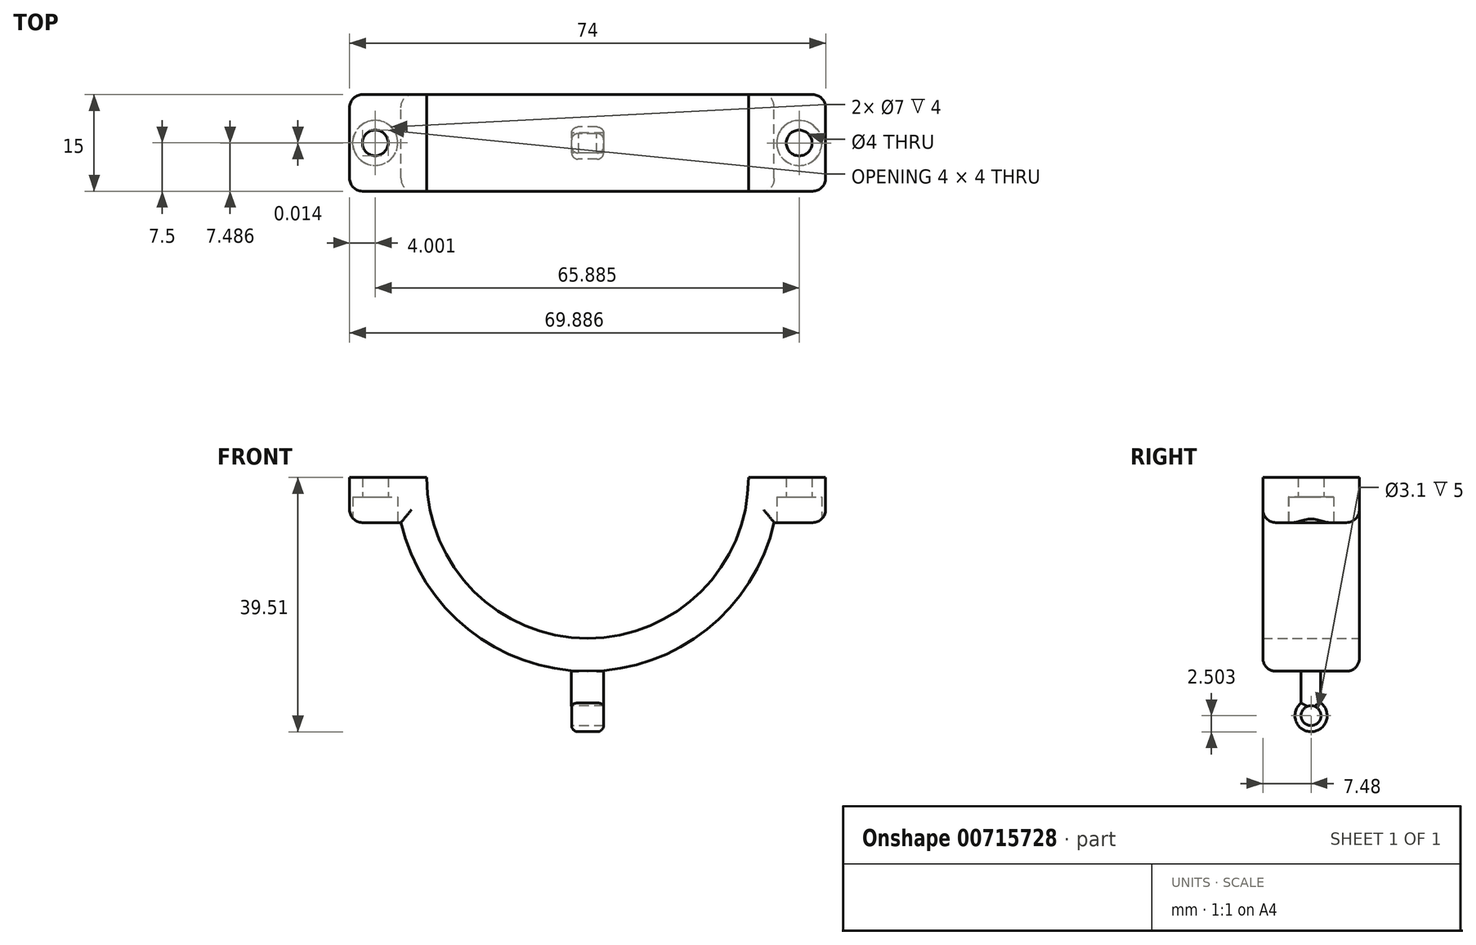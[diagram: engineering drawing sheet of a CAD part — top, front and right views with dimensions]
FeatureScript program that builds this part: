
annotation { "Feature Type Name" : "Feature", "Feature Type Description" : "" }
export const myFeature = defineFeature(function(context is Context, id is Id, definition is map)
    precondition{}
    {
        {
            var Q0;
            Q0=qCreatedBy(makeId("Front.planeOp"),FACE);
            var sketch = newSketch(context, id + "F0", { "sketchPlane" : qUnion([Q0])});
            skArc(sketch, "E0", {"start": v(-25, 0.05) * mm, "mid": v(0, -24.95) * mm, "end": v(25, 0.05) * mm});
            skLineSegment(sketch, "E1", {"start": v(-25, 0.05) * mm, "end": v(-37, 0.05) * mm});
            skLineSegment(sketch, "E2", {"start": v(-37, 0.05) * mm, "end": v(-37, -6.95) * mm});
            skLineSegment(sketch, "E3", {"start": v(-37, -6.95) * mm, "end": v(-29, -6.95) * mm});
            skLineSegment(sketch, "E4", {"start": v(25, 0.05) * mm, "end": v(37, 0.05) * mm});
            skLineSegment(sketch, "E5", {"start": v(37, 0.05) * mm, "end": v(37, -6.95) * mm});
            skLineSegment(sketch, "E6", {"start": v(37, -6.95) * mm, "end": v(29, -6.95) * mm});
            skArc(sketch, "E7", {"start": v(-29, -6.95) * mm, "mid": v(0, -30.05) * mm, "end": v(29, -6.95) * mm});
            skSolve(sketch);
        }
        {
            var Q0;
            Q0=makeQuery(id+"F0.imprint","IMPRINT",FACE,{"disambiguationData":[TD([[makeQuery(id+"F0.imprint","IMPRINT",EDGE,{"derivedFrom":sQuery(id+"F0.wireOp",EDGE,"E0")}),-1.0]])]});
            extrude(context, id + "F1", {"entities" : qUnion([Q0]), "depth" : 15 * mm, "offsetDistance" : 25 * mm});
        }
        {
            var Q0;
            Q0=makeQuery(id+"F1.opExtrude","SWEPT_EDGE",EDGE,{"disambiguationData":[OSD([sQuery(id+"F0.wireOp",EDGE,"E5"),sQuery(id+"F0.wireOp",EDGE,"E6")])]});
            var Q1;
            Q1=makeQuery(id+"F1.opExtrude","SWEPT_EDGE",EDGE,{"disambiguationData":[OSD([sQuery(id+"F0.wireOp",EDGE,"E2"),sQuery(id+"F0.wireOp",EDGE,"E3")])]});
            fillet(context, id + "F2", {"entities" : qUnion([Q0, Q1]), "radius" : 2 * mm, "tangentPropagation" : true, "allowEdgeOverflow" : false});
        }
        {
            var Q0;
            Q0=makeQuery(id+"F1.opExtrude","CAP_EDGE",EDGE,{"disambiguationData":[OSD([sQuery(id+"F0.wireOp",EDGE,"E6")])],"isStart":false});
            var Q1;
            Q1=makeQuery(id+"F1.opExtrude","CAP_EDGE",EDGE,{"disambiguationData":[OSD([sQuery(id+"F0.wireOp",EDGE,"E7")])],"isStart":false});
            var Q2;
            Q2=makeQuery(id+"F1.opExtrude","CAP_EDGE",EDGE,{"disambiguationData":[OSD([sQuery(id+"F0.wireOp",EDGE,"E3")])],"isStart":false});
            var Q3;
            {var subQ0=sQuery(id+"F0.wireOp",EDGE,"E3");var subQ1=sQuery(id+"F0.wireOp",EDGE,"E2");Q3=makeQuery(id+"F2.opFillet","BLEND_EDGE",EDGE,{"blendedFrom":[makeQuery(id+"F1.opExtrude","SWEPT_EDGE",EDGE,{"disambiguationData":[OSD([subQ1,subQ0])]}),makeQuery(id+"F1.opExtrude","CAP_FACE",FACE,{"disambiguationData":[OSD([sQuery(id+"F0.wireOp",EDGE,"E0"),sQuery(id+"F0.wireOp",EDGE,"E1"),subQ1,subQ0,sQuery(id+"F0.wireOp",EDGE,"E4"),sQuery(id+"F0.wireOp",EDGE,"E5"),sQuery(id+"F0.wireOp",EDGE,"E6"),sQuery(id+"F0.wireOp",EDGE,"E7")])],"isStart":false})],"blendedInto":[makeQuery(id+"F1.opExtrude","CAP_FACE",FACE,{"disambiguationData":[OSD([sQuery(id+"F0.wireOp",EDGE,"E0"),sQuery(id+"F0.wireOp",EDGE,"E1"),subQ1,subQ0,sQuery(id+"F0.wireOp",EDGE,"E4"),sQuery(id+"F0.wireOp",EDGE,"E5"),sQuery(id+"F0.wireOp",EDGE,"E6"),sQuery(id+"F0.wireOp",EDGE,"E7")])],"isStart":false})]});}
            var Q4;
            Q4=makeQuery(id+"F1.opExtrude","CAP_EDGE",EDGE,{"disambiguationData":[OSD([sQuery(id+"F0.wireOp",EDGE,"E2")])],"isStart":false});
            var Q5;
            {var subQ0=sQuery(id+"F0.wireOp",EDGE,"E6");var subQ1=sQuery(id+"F0.wireOp",EDGE,"E5");Q5=makeQuery(id+"F2.opFillet","BLEND_EDGE",EDGE,{"blendedFrom":[makeQuery(id+"F1.opExtrude","SWEPT_EDGE",EDGE,{"disambiguationData":[OSD([subQ1,subQ0])]}),makeQuery(id+"F1.opExtrude","CAP_FACE",FACE,{"disambiguationData":[OSD([sQuery(id+"F0.wireOp",EDGE,"E0"),sQuery(id+"F0.wireOp",EDGE,"E1"),sQuery(id+"F0.wireOp",EDGE,"E2"),sQuery(id+"F0.wireOp",EDGE,"E3"),sQuery(id+"F0.wireOp",EDGE,"E4"),subQ1,subQ0,sQuery(id+"F0.wireOp",EDGE,"E7")])],"isStart":false})],"blendedInto":[makeQuery(id+"F1.opExtrude","CAP_FACE",FACE,{"disambiguationData":[OSD([sQuery(id+"F0.wireOp",EDGE,"E0"),sQuery(id+"F0.wireOp",EDGE,"E1"),sQuery(id+"F0.wireOp",EDGE,"E2"),sQuery(id+"F0.wireOp",EDGE,"E3"),sQuery(id+"F0.wireOp",EDGE,"E4"),subQ1,subQ0,sQuery(id+"F0.wireOp",EDGE,"E7")])],"isStart":false})]});}
            var Q6;
            Q6=makeQuery(id+"F1.opExtrude","CAP_EDGE",EDGE,{"disambiguationData":[OSD([sQuery(id+"F0.wireOp",EDGE,"E5")])],"isStart":false});
            fillet(context, id + "F3", {"entities" : qUnion([Q0, Q1, Q2, Q3, Q4, Q5, Q6]), "radius" : 2 * mm, "tangentPropagation" : true, "allowEdgeOverflow" : false});
        }
        {
            var Q0;
            Q0=makeQuery(id+"F1.opExtrude","CAP_EDGE",EDGE,{"disambiguationData":[OSD([sQuery(id+"F0.wireOp",EDGE,"E7")])],"isStart":true});
            var Q1;
            Q1=makeQuery(id+"F1.opExtrude","CAP_EDGE",EDGE,{"disambiguationData":[OSD([sQuery(id+"F0.wireOp",EDGE,"E3")])],"isStart":true});
            var Q2;
            {var subQ0=sQuery(id+"F0.wireOp",EDGE,"E3");var subQ1=sQuery(id+"F0.wireOp",EDGE,"E2");Q2=makeQuery(id+"F2.opFillet","BLEND_EDGE",EDGE,{"blendedFrom":[makeQuery(id+"F1.opExtrude","SWEPT_EDGE",EDGE,{"disambiguationData":[OSD([subQ1,subQ0])]}),makeQuery(id+"F1.opExtrude","CAP_FACE",FACE,{"disambiguationData":[OSD([sQuery(id+"F0.wireOp",EDGE,"E0"),sQuery(id+"F0.wireOp",EDGE,"E1"),subQ1,subQ0,sQuery(id+"F0.wireOp",EDGE,"E4"),sQuery(id+"F0.wireOp",EDGE,"E5"),sQuery(id+"F0.wireOp",EDGE,"E6"),sQuery(id+"F0.wireOp",EDGE,"E7")])],"isStart":true})],"blendedInto":[makeQuery(id+"F1.opExtrude","CAP_FACE",FACE,{"disambiguationData":[OSD([sQuery(id+"F0.wireOp",EDGE,"E0"),sQuery(id+"F0.wireOp",EDGE,"E1"),subQ1,subQ0,sQuery(id+"F0.wireOp",EDGE,"E4"),sQuery(id+"F0.wireOp",EDGE,"E5"),sQuery(id+"F0.wireOp",EDGE,"E6"),sQuery(id+"F0.wireOp",EDGE,"E7")])],"isStart":true})]});}
            var Q3;
            Q3=makeQuery(id+"F1.opExtrude","CAP_EDGE",EDGE,{"disambiguationData":[OSD([sQuery(id+"F0.wireOp",EDGE,"E2")])],"isStart":true});
            var Q4;
            Q4=makeQuery(id+"F1.opExtrude","CAP_EDGE",EDGE,{"disambiguationData":[OSD([sQuery(id+"F0.wireOp",EDGE,"E6")])],"isStart":true});
            var Q5;
            {var subQ0=sQuery(id+"F0.wireOp",EDGE,"E6");var subQ1=sQuery(id+"F0.wireOp",EDGE,"E5");Q5=makeQuery(id+"F2.opFillet","BLEND_EDGE",EDGE,{"blendedFrom":[makeQuery(id+"F1.opExtrude","SWEPT_EDGE",EDGE,{"disambiguationData":[OSD([subQ1,subQ0])]}),makeQuery(id+"F1.opExtrude","CAP_FACE",FACE,{"disambiguationData":[OSD([sQuery(id+"F0.wireOp",EDGE,"E0"),sQuery(id+"F0.wireOp",EDGE,"E1"),sQuery(id+"F0.wireOp",EDGE,"E2"),sQuery(id+"F0.wireOp",EDGE,"E3"),sQuery(id+"F0.wireOp",EDGE,"E4"),subQ1,subQ0,sQuery(id+"F0.wireOp",EDGE,"E7")])],"isStart":true})],"blendedInto":[makeQuery(id+"F1.opExtrude","CAP_FACE",FACE,{"disambiguationData":[OSD([sQuery(id+"F0.wireOp",EDGE,"E0"),sQuery(id+"F0.wireOp",EDGE,"E1"),sQuery(id+"F0.wireOp",EDGE,"E2"),sQuery(id+"F0.wireOp",EDGE,"E3"),sQuery(id+"F0.wireOp",EDGE,"E4"),subQ1,subQ0,sQuery(id+"F0.wireOp",EDGE,"E7")])],"isStart":true})]});}
            var Q6;
            Q6=makeQuery(id+"F1.opExtrude","CAP_EDGE",EDGE,{"disambiguationData":[OSD([sQuery(id+"F0.wireOp",EDGE,"E5")])],"isStart":true});
            fillet(context, id + "F4", {"entities" : qUnion([Q0, Q1, Q2, Q3, Q4, Q5, Q6]), "radius" : 2 * mm, "tangentPropagation" : true, "allowEdgeOverflow" : false});
        }
        {
            var Q0;
            Q0=makeQuery(id+"F1.opExtrude","SWEPT_FACE",FACE,{"disambiguationData":[OSD([sQuery(id+"F0.wireOp",EDGE,"E6")])]});
            var sketch = newSketch(context, id + "F5", { "sketchPlane" : qUnion([Q0])});
            skCircle(sketch, "E8", {"center": v(32.89, 7.51) * mm, "radius": 2 * mm});
            skCircle(sketch, "E9", {"center": v(32.89, 7.51) * mm, "radius": 3.5 * mm});
            skSolve(sketch);
        }
        {
            var Q0;
            Q0=makeQuery(id+"F5.imprint","IMPRINT",FACE,{"disambiguationData":[TD([[makeQuery(id+"F5.imprint","IMPRINT",EDGE,{"derivedFrom":sQuery(id+"F5.wireOp",EDGE,"E8")}),1.0]])]});
            extrude(context, id + "F6", {"entities" : qUnion([Q0]), "operationType" : NewBodyOperationType.REMOVE, "oppositeDirection" : true, "depth" : 25 * mm, "offsetDistance" : 25 * mm});
        }
        {
            var Q0;
            Q0=makeQuery(id+"F5.imprint","IMPRINT",FACE,{"disambiguationData":[TD([[makeQuery(id+"F5.imprint","IMPRINT",EDGE,{"derivedFrom":sQuery(id+"F5.wireOp",EDGE,"E8")}),-1.0]])]});
            var Q1;
            {var subQ0=sQuery(id+"F5.wireOp",EDGE,"E9");var subQ1=sQuery(id+"F0.wireOp",EDGE,"E6");var subQ2=makeQuery(id+"F2.opFillet","BLEND_EDGE",EDGE,{"blendedFrom":[makeQuery(id+"F1.opExtrude","SWEPT_EDGE",EDGE,{"disambiguationData":[OSD([sQuery(id+"F0.wireOp",EDGE,"E5"),subQ1])]}),makeQuery(id+"F1.opExtrude","SWEPT_FACE",FACE,{"disambiguationData":[OSD([subQ1])]})],"blendedInto":[makeQuery(id+"F1.opExtrude","SWEPT_FACE",FACE,{"disambiguationData":[OSD([subQ1])]})]});var subQ3=makeQuery(id+"F5.imprint","INTERSECT",VERTEX,{"disambiguationData":[OD(0.0)],"derivedFrom":[subQ2,subQ0]});Q1=makeQuery(id+"F5.imprint","IMPRINT",FACE,{"disambiguationData":[TD([[makeQuery(id+"F5.imprint","IMPRINT",EDGE,{"disambiguationData":[TD([[subQ3,1.0]])],"derivedFrom":subQ0}),1.0]])]});}
            extrude(context, id + "F7", {"entities" : qUnion([Q0, Q1]), "operationType" : NewBodyOperationType.REMOVE, "oppositeDirection" : true, "depth" : 4 * mm, "offsetDistance" : 25 * mm});
        }
        {
            var Q0;
            Q0=makeQuery(id+"F1.opExtrude","SWEPT_FACE",FACE,{"disambiguationData":[OSD([sQuery(id+"F0.wireOp",EDGE,"E3")])]});
            var sketch = newSketch(context, id + "F8", { "sketchPlane" : qUnion([Q0])});
            skCircle(sketch, "E10", {"center": v(-33, 7.5) * mm, "radius": 2 * mm});
            skCircle(sketch, "E11", {"center": v(-33, 7.5) * mm, "radius": 3.5 * mm});
            skSolve(sketch);
        }
        {
            var Q0;
            {var subQ0=sQuery(id+"F8.wireOp",EDGE,"E10");var subQ1=sQuery(id+"F0.wireOp",EDGE,"E3");var subQ2=makeQuery(id+"F2.opFillet","BLEND_EDGE",EDGE,{"blendedFrom":[makeQuery(id+"F1.opExtrude","SWEPT_EDGE",EDGE,{"disambiguationData":[OSD([sQuery(id+"F0.wireOp",EDGE,"E2"),subQ1])]}),makeQuery(id+"F1.opExtrude","SWEPT_FACE",FACE,{"disambiguationData":[OSD([subQ1])]})],"blendedInto":[makeQuery(id+"F1.opExtrude","SWEPT_FACE",FACE,{"disambiguationData":[OSD([subQ1])]})]});var subQ3=makeQuery(id+"F8.imprint","INTERSECT",VERTEX,{"disambiguationData":[OD(0.0)],"derivedFrom":[subQ2,subQ0]});Q0=makeQuery(id+"F8.imprint","IMPRINT",FACE,{"disambiguationData":[TD([[makeQuery(id+"F8.imprint","IMPRINT",EDGE,{"disambiguationData":[TD([[subQ3,-1.0]])],"derivedFrom":subQ0}),1.0]])]});}
            extrude(context, id + "F9", {"entities" : qUnion([Q0]), "operationType" : NewBodyOperationType.REMOVE, "oppositeDirection" : true, "depth" : 25 * mm, "offsetDistance" : 25 * mm});
        }
        {
            var Q0;
            {var subQ0=sQuery(id+"F8.wireOp",EDGE,"E10");var subQ1=sQuery(id+"F0.wireOp",EDGE,"E3");var subQ2=makeQuery(id+"F2.opFillet","BLEND_EDGE",EDGE,{"blendedFrom":[makeQuery(id+"F1.opExtrude","SWEPT_EDGE",EDGE,{"disambiguationData":[OSD([sQuery(id+"F0.wireOp",EDGE,"E2"),subQ1])]}),makeQuery(id+"F1.opExtrude","SWEPT_FACE",FACE,{"disambiguationData":[OSD([subQ1])]})],"blendedInto":[makeQuery(id+"F1.opExtrude","SWEPT_FACE",FACE,{"disambiguationData":[OSD([subQ1])]})]});var subQ3=makeQuery(id+"F8.imprint","INTERSECT",VERTEX,{"disambiguationData":[OD(0.0)],"derivedFrom":[subQ2,subQ0]});Q0=makeQuery(id+"F8.imprint","IMPRINT",FACE,{"disambiguationData":[TD([[makeQuery(id+"F8.imprint","IMPRINT",EDGE,{"disambiguationData":[TD([[subQ3,1.0]])],"derivedFrom":subQ0}),-1.0]])]});}
            var Q1;
            {var subQ0=sQuery(id+"F8.wireOp",EDGE,"E10");var subQ1=sQuery(id+"F0.wireOp",EDGE,"E3");var subQ2=makeQuery(id+"F2.opFillet","BLEND_EDGE",EDGE,{"blendedFrom":[makeQuery(id+"F1.opExtrude","SWEPT_EDGE",EDGE,{"disambiguationData":[OSD([sQuery(id+"F0.wireOp",EDGE,"E2"),subQ1])]}),makeQuery(id+"F1.opExtrude","SWEPT_FACE",FACE,{"disambiguationData":[OSD([subQ1])]})],"blendedInto":[makeQuery(id+"F1.opExtrude","SWEPT_FACE",FACE,{"disambiguationData":[OSD([subQ1])]})]});var subQ3=makeQuery(id+"F8.imprint","INTERSECT",VERTEX,{"disambiguationData":[OD(0.0)],"derivedFrom":[subQ2,subQ0]});Q1=makeQuery(id+"F8.imprint","IMPRINT",FACE,{"disambiguationData":[TD([[makeQuery(id+"F8.imprint","IMPRINT",EDGE,{"disambiguationData":[TD([[subQ3,-1.0]])],"derivedFrom":subQ0}),-1.0]])]});}
            extrude(context, id + "F10", {"entities" : qUnion([Q0, Q1]), "operationType" : NewBodyOperationType.REMOVE, "oppositeDirection" : true, "depth" : 4 * mm, "offsetDistance" : 25 * mm});
        }
        {
            var Q0;
            Q0=qCreatedBy(makeId("Right.planeOp"),FACE);
            var sketch = newSketch(context, id + "F11", { "sketchPlane" : qUnion([Q0])});
            skLineSegment(sketch, "E12.bottom", {"start": v(-6.06, -30.02) * mm, "end": v(-9.06, -30.02) * mm});
            skLineSegment(sketch, "E12.top", {"start": v(-6.06, -35.02) * mm, "end": v(-9.06, -35.02) * mm});
            skLineSegment(sketch, "E12.left", {"start": v(-6.06, -30.02) * mm, "end": v(-6.06, -35.02) * mm});
            skLineSegment(sketch, "E12.right", {"start": v(-9.06, -30.02) * mm, "end": v(-9.06, -35.02) * mm});
            skCircle(sketch, "E13", {"center": v(-7.52, -36.96) * mm, "radius": 2.5 * mm});
            skCircle(sketch, "E14", {"center": v(-7.52, -36.96) * mm, "radius": 1.55 * mm});
            skSolve(sketch);
        }
        {
            var Q0;
            {var subQ0=sQuery(id+"F11.wireOp",EDGE,"E12.top");Q0=makeQuery(id+"F11.imprint","IMPRINT",FACE,{"disambiguationData":[TD([[makeQuery(id+"F11.imprint","IMPRINT",EDGE,{"derivedFrom":subQ0}),1.0]])]});}
            var Q1;
            {var subQ0=sQuery(id+"F11.wireOp",EDGE,"E12.bottom");Q1=makeQuery(id+"F11.imprint","IMPRINT",FACE,{"disambiguationData":[TD([[makeQuery(id+"F11.imprint","IMPRINT",EDGE,{"derivedFrom":subQ0}),1.0]])]});}
            var Q2;
            {var subQ0=sQuery(id+"F11.wireOp",EDGE,"E12.top");Q2=makeQuery(id+"F11.imprint","IMPRINT",FACE,{"disambiguationData":[TD([[makeQuery(id+"F11.imprint","IMPRINT",EDGE,{"derivedFrom":subQ0}),-1.0]])]});}
            extrude(context, id + "F12", {"entities" : qUnion([Q0, Q1, Q2]), "operationType" : NewBodyOperationType.ADD, "endBound" : BoundingType.SYMMETRIC, "depth" : 5 * mm, "offsetDistance" : 25 * mm});
        }
        {
            var Q0;
            Q0=makeQuery(id+"F12.opExtrude","CAP_EDGE",EDGE,{"disambiguationData":[OSD([sQuery(id+"F11.wireOp",EDGE,"E13")])],"isStart":false});
            var Q1;
            Q1=makeQuery(id+"F12.opExtrude","CAP_EDGE",EDGE,{"disambiguationData":[OSD([sQuery(id+"F11.wireOp",EDGE,"E12.right")])],"isStart":false});
            var Q2;
            Q2=makeQuery(id+"F12.opExtrude","CAP_EDGE",EDGE,{"disambiguationData":[OSD([sQuery(id+"F11.wireOp",EDGE,"E12.left")])],"isStart":false});
            var Q3;
            Q3=makeQuery(id+"F12.opExtrude","CAP_EDGE",EDGE,{"disambiguationData":[OSD([sQuery(id+"F11.wireOp",EDGE,"E13")])],"isStart":true});
            var Q4;
            Q4=makeQuery(id+"F12.opExtrude","CAP_EDGE",EDGE,{"disambiguationData":[OSD([sQuery(id+"F11.wireOp",EDGE,"E12.right")])],"isStart":true});
            var Q5;
            Q5=makeQuery(id+"F12.opExtrude","CAP_EDGE",EDGE,{"disambiguationData":[OSD([sQuery(id+"F11.wireOp",EDGE,"E12.left")])],"isStart":true});
            fillet(context, id + "F13", {"entities" : qUnion([Q0, Q1, Q2, Q3, Q4, Q5]), "radius" : 1 * mm, "tangentPropagation" : true, "allowEdgeOverflow" : false});
        }
    });
